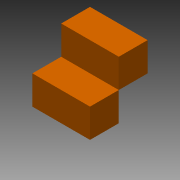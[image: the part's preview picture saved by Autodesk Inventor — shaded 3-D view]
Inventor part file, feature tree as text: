
AUTODESK INVENTOR PART (.ipt)
format: ipt  version: 2013 (Build 170138000, 138)  size: 109,056 bytes
history: native  units: in
note: dims shown in document units (in); Inventor stores cm internally (conversion verified against a paired STEP export)
features: extrude x4, sketch x4
ambient origin geometry x8: Origin, YZ Plane, XZ Plane, XY Plane, X Axis, Y Axis, Z Axis, Center Point
bodies: Solid1 (feature_tree)
feature tree (8):
  extrude  "Extrusion1"  Depth=0.75in
  extrude  "Extrusion2"  Depth=0.75in
  extrude  "Extrusion3"  Depth=0.75in TaperAngle=0.0deg
  extrude  "Extrusion4"  [1 undecoded]
  sketch  "Sketch1"  dims[d0=2.25in d1=0.75in]
  sketch  "Sketch2"  dims[d2=0.75in d3=0.0in d4=0.75in]
  sketch  "Sketch3"  dims[d5=0.75in d6=0.0in d7=0.75in d8=0.0in]
  sketch  "Sketch4"  dims[d9=0.75in d10=0.0in]
note: 1 required parameter value undecoded (feature->parameter linkage not recoverable at this tier; creation-order binding heuristic only, values carry confidence <= 0.55)
